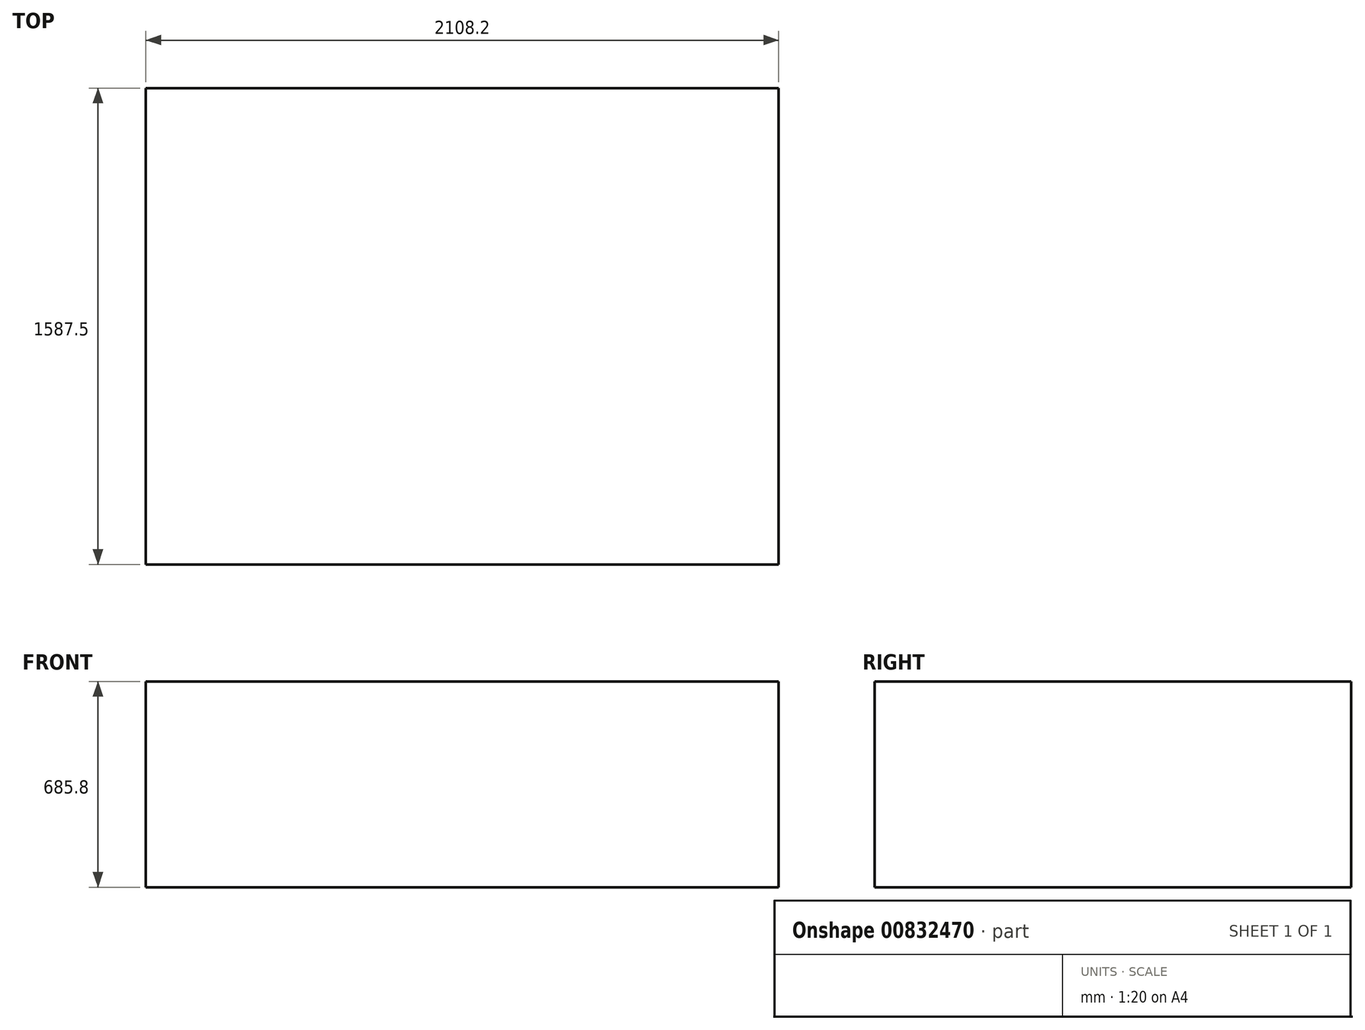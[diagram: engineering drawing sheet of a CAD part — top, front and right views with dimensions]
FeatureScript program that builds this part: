
annotation { "Feature Type Name" : "Feature", "Feature Type Description" : "" }
export const myFeature = defineFeature(function(context is Context, id is Id, definition is map)
    precondition{}
    {
        {
            var Q0;
            Q0=qCreatedBy(makeId("Top.planeOp"),FACE);
            var sketch = newSketch(context, id + "F0", { "sketchPlane" : qUnion([Q0])});
            skLineSegment(sketch, "E0.bottom", {"start": v(0, 0) * mm, "end": v(2108.2, 0) * mm});
            skLineSegment(sketch, "E0.top", {"start": v(0, 1587.5) * mm, "end": v(2108.2, 1587.5) * mm});
            skLineSegment(sketch, "E0.left", {"start": v(0, 0) * mm, "end": v(0, 1587.5) * mm});
            skLineSegment(sketch, "E0.right", {"start": v(2108.2, 0) * mm, "end": v(2108.2, 1587.5) * mm});
            skSolve(sketch);
        }
        {
            var Q0;
            Q0 = qSketchRegion(id + "F0", true);
            extrude(context, id + "F1", {"entities" : qUnion([Q0]), "depth" : 685.8 * mm, "offsetDistance" : 25.4 * mm});
        }
    });
